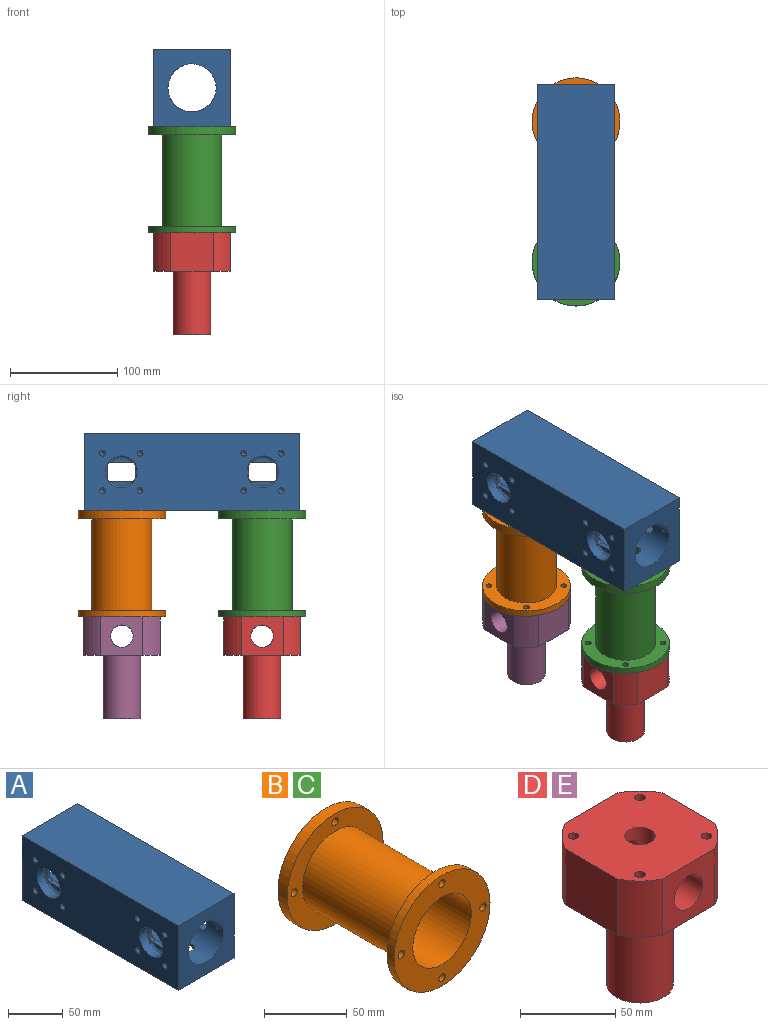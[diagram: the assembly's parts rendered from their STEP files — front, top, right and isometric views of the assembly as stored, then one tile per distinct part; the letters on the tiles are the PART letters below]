
ASSEMBLY  parts=5 mates=10
PART A: 165 faces, bbox 72.3x201.3x72.3 mm
  f0: cylinder r=22.5mm len=201mm, axis (0,-1,0), area 25576.7mm2, adj f1,f114,f115,f116,f117,f118,f119,f120
  f1: cone r=0mm half-angle=59deg, axis (1,0,0), area 3.6mm2, adj f0,f2
  f2: cylinder r=1mm len=10mm, axis (1,0,0), area 62.8mm2, adj f1,f3
  f3: cone r=1mm half-angle=45deg, axis (1,0,0), area 66.6mm2, adj f2,f4
  f4: plane 201.02x72.02mm, normal (1,0,0), area 12119.6mm2, adj f3,f5,f85,f86,f87,f88,f89,f90
  f5: plane 201x72mm, normal (0,0,-1), area 9355.9mm2, adj f4,f6,f53,f58,f63,f65,f67,f69
  f6: plane 201x72mm, normal (-1,0,0), area 12868.2mm2, adj f5,f7,f22,f37,f39,f41,f43,f45
  f7: cylinder r=15mm len=30mm, axis (-1,0,0), area 862.6mm2, adj f6,f8,f9,f11,f12,f13,f14,f15
  f8: bspline ~2.82x2.43mm, area 2.1mm2, adj f7,f9,f21,f159
  f9: torus R=13mm, axis (-1,0,0), area 72.2mm2, adj f7,f8,f10,f11
  f10: plane 18.74x3.99mm, normal (-1,0,0), area 51.6mm2, adj f9,f159
  f11: bspline ~2.87x2.49mm, area 2.1mm2, adj f7,f9,f12,f159
  f12: bspline ~3.64x3.35mm, area 6.1mm2, adj f7,f11,f13,f158
  f13: bspline ~14.54x2mm, area 35.1mm2, adj f7,f12,f14,f157
  f14: bspline ~3.66x3.36mm, area 6.2mm2, adj f7,f13,f15,f156
  f15: bspline ~2.82x2.43mm, area 2mm2, adj f7,f14,f16,f155
  f16: torus R=13mm, axis (-1,0,0), area 72.4mm2, adj f7,f15,f17,f18
  f17: plane 18.78x4.01mm, normal (-1,0,0), area 52mm2, adj f16,f155
  f18: bspline ~2.86x2.49mm, area 2mm2, adj f7,f16,f19,f155
  f19: bspline ~3.66x3.36mm, area 6.2mm2, adj f7,f18,f20,f162
  f20: bspline ~14.54x2mm, area 35.1mm2, adj f7,f19,f21,f161
  f21: bspline ~4.35x3.75mm, area 6.1mm2, adj f7,f8,f20,f160
  f22: cylinder r=15mm len=30mm, axis (-1,0,0), area 862.6mm2, adj f6,f23,f24,f26,f27,f28,f29,f30
  f23: bspline ~2.82x2.43mm, area 2.1mm2, adj f22,f24,f36,f140
  f24: torus R=13mm, axis (-1,0,0), area 72.2mm2, adj f22,f23,f25,f26
  f25: plane 18.74x3.99mm, normal (-1,0,0), area 51.6mm2, adj f24,f140
  f26: bspline ~2.87x2.49mm, area 2.1mm2, adj f22,f24,f27,f140
  f27: bspline ~3.64x3.35mm, area 6.1mm2, adj f22,f26,f28,f139
  f28: bspline ~14.54x2mm, area 35.1mm2, adj f22,f27,f29,f146
  f29: bspline ~3.66x3.36mm, area 6.2mm2, adj f22,f28,f30,f145
  f30: bspline ~2.82x2.43mm, area 2mm2, adj f22,f29,f31,f144
  f31: torus R=13mm, axis (-1,0,0), area 72.4mm2, adj f22,f30,f32,f33
  f32: plane 18.78x4.01mm, normal (-1,0,0), area 52mm2, adj f31,f144
  f33: bspline ~2.86x2.49mm, area 2mm2, adj f22,f31,f34,f144
  f34: bspline ~3.66x3.36mm, area 6.2mm2, adj f22,f33,f35,f143
  f35: bspline ~14.54x2mm, area 35.1mm2, adj f22,f34,f36,f142
  f36: bspline ~4.35x3.75mm, area 6.1mm2, adj f22,f23,f35,f141
  f37: cylinder r=2.75mm len=13mm, axis (-1,0,0), area 224.6mm2, adj f6,f38
  f38: cone r=0mm half-angle=59deg, axis (-1,0,0), area 27.7mm2, adj f37
  f39: cylinder r=2.75mm len=13mm, axis (-1,0,0), area 224.6mm2, adj f6,f40
  f40: cone r=0mm half-angle=59deg, axis (-1,0,0), area 27.7mm2, adj f39
  f41: cylinder r=2.75mm len=13mm, axis (-1,0,0), area 224.6mm2, adj f6,f42
  f42: cone r=0mm half-angle=59deg, axis (-1,0,0), area 27.7mm2, adj f41
  f43: cylinder r=2.75mm len=13mm, axis (-1,0,0), area 224.6mm2, adj f6,f44
  f44: cone r=0mm half-angle=59deg, axis (-1,0,0), area 27.7mm2, adj f43
  f45: cylinder r=2.75mm len=13mm, axis (-1,0,0), area 224.6mm2, adj f6,f46
  f46: cone r=0mm half-angle=59deg, axis (-1,0,0), area 27.7mm2, adj f45
  f47: cylinder r=2.75mm len=13mm, axis (-1,0,0), area 224.6mm2, adj f6,f48
  f48: cone r=0mm half-angle=59deg, axis (-1,0,0), area 27.7mm2, adj f47
  f49: cylinder r=2.75mm len=13mm, axis (-1,0,0), area 224.6mm2, adj f6,f50
  f50: cone r=0mm half-angle=59deg, axis (-1,0,0), area 27.7mm2, adj f49
  f51: cylinder r=2.75mm len=13mm, axis (-1,0,0), area 224.6mm2, adj f6,f52
  f52: cone r=0mm half-angle=59deg, axis (-1,0,0), area 27.7mm2, adj f51
  f53: cylinder r=28mm len=56mm, axis (0,0,-1), area 439.8mm2, adj f5,f54
  f54: plane 56x56mm, normal (0,0,-1), area 87.2mm2, adj f53,f55
  f55: torus R=26mm, axis (0,0,-1), area 769.8mm2, adj f54,f56
  f56: plane 49x49mm, normal (0,0,-1), area 382.9mm2, adj f55,f57
  f57: cone r=24.52mm half-angle=46.5deg, axis (0,0,-1), area 1437.8mm2, adj f56,f131,f132,f133,f134,f135,f136,f137
  f58: cylinder r=28mm len=56mm, axis (0,0,-1), area 439.8mm2, adj f5,f59
  f59: plane 56x56mm, normal (0,0,-1), area 87.2mm2, adj f58,f60
  f60: torus R=26mm, axis (0,0,-1), area 769.8mm2, adj f59,f61
  f61: plane 49x49mm, normal (0,0,-1), area 382.9mm2, adj f60,f62
  f62: cone r=24.52mm half-angle=46.5deg, axis (0,0,-1), area 1437.8mm2, adj f61,f123,f124,f125,f126,f127,f128,f129
  f63: cylinder r=2.75mm len=15mm, axis (0,0,-1), area 224.6mm2, adj f5,f64,f99
  f64: cone r=0mm half-angle=59deg, axis (0,0,-1), area 23.4mm2, adj f63,f99
  f65: cylinder r=2.75mm len=15mm, axis (0,0,-1), area 259.2mm2, adj f5,f66
  f66: cone r=0mm half-angle=59deg, axis (0,0,-1), area 27.7mm2, adj f65
  f67: cylinder r=2.75mm len=15mm, axis (0,0,-1), area 259.2mm2, adj f5,f68
  f68: cone r=0mm half-angle=59deg, axis (0,0,-1), area 27.7mm2, adj f67
  f69: cylinder r=2.75mm len=15mm, axis (0,0,-1), area 203.8mm2, adj f5,f70,f72,f73,f98
  f70: cone r=0mm half-angle=59deg, axis (0,0,-1), area 19mm2, adj f69,f71,f98
  f71: cylinder r=2.75mm len=2.49mm, axis (0,0,-1), area 0mm2, adj f70,f98
  f72: cylinder r=2.75mm len=0.48mm, axis (1,0,0), area 0mm2, adj f69,f73,f98
  f73: cone r=0mm half-angle=59deg, axis (1,0,0), area 27.7mm2, adj f69,f72,f98
  f74: cylinder r=2.75mm len=15mm, axis (0,0,-1), area 224.6mm2, adj f5,f75,f101
  f75: cone r=0mm half-angle=59deg, axis (0,0,-1), area 23.4mm2, adj f74,f101
  f76: cylinder r=2.75mm len=15mm, axis (0,0,-1), area 259.2mm2, adj f5,f77
  f77: cone r=0mm half-angle=59deg, axis (0,0,-1), area 27.7mm2, adj f76
  f78: cylinder r=2.75mm len=15mm, axis (0,0,-1), area 259.2mm2, adj f5,f79
  f79: cone r=0mm half-angle=59deg, axis (0,0,-1), area 27.7mm2, adj f78
  f80: cylinder r=2.75mm len=15mm, axis (0,0,-1), area 203.8mm2, adj f5,f81,f82,f84,f103
  f81: cylinder r=2.75mm len=0.48mm, axis (1,0,0), area 0mm2, adj f80,f84,f103
  f82: cone r=0mm half-angle=59deg, axis (0,0,-1), area 19mm2, adj f80,f83,f103
  f83: cylinder r=2.75mm len=2.49mm, axis (0,0,-1), area 0mm2, adj f82,f103
  f84: cone r=0mm half-angle=59deg, axis (1,0,0), area 27.7mm2, adj f80,f81,f103
  f85: plane 201x72mm, normal (0,0,1), area 14472mm2, adj f4,f6,f163,f164
  f86: cone r=17.5mm half-angle=43.4deg, axis (1,0,0), area 730.9mm2, adj f4,f87,f147,f148,f149,f150,f151,f152
  f87: cone r=17.5mm half-angle=48.8deg, axis (1,0,0), area 0mm2, adj f4,f86
  f88: cone r=17.5mm half-angle=43.4deg, axis (1,0,0), area 730.9mm2, adj f4,f89,f115,f116,f117,f118,f119,f120
  f89: cone r=17.5mm half-angle=48.8deg, axis (1,0,0), area 0mm2, adj f4,f88
  f90: cylinder r=2.75mm len=14mm, axis (1,0,0), area 241.9mm2, adj f4,f91
  f91: cone r=0mm half-angle=59deg, axis (1,0,0), area 27.7mm2, adj f90
  f92: cylinder r=2.75mm len=14mm, axis (1,0,0), area 241.9mm2, adj f4,f93
  f93: cone r=0mm half-angle=59deg, axis (1,0,0), area 27.7mm2, adj f92
  f94: cylinder r=2.75mm len=14mm, axis (1,0,0), area 241.9mm2, adj f4,f95
  f95: cone r=0mm half-angle=59deg, axis (1,0,0), area 27.7mm2, adj f94
  f96: cylinder r=2.75mm len=14mm, axis (1,0,0), area 241.9mm2, adj f4,f97
  f97: cone r=0mm half-angle=59deg, axis (1,0,0), area 27.7mm2, adj f96
  f98: cylinder r=2.75mm len=14mm, axis (1,0,0), area 191mm2, adj f4,f69,f70,f71,f72,f73
  f99: cylinder r=2.75mm len=14mm, axis (1,0,0), area 207.5mm2, adj f4,f63,f64,f100
  f100: cone r=0mm half-angle=59deg, axis (1,0,0), area 27.7mm2, adj f99
  f101: cylinder r=2.75mm len=14mm, axis (1,0,0), area 207.4mm2, adj f4,f74,f75,f102
  f102: cone r=0mm half-angle=59deg, axis (1,0,0), area 27.7mm2, adj f101
  f103: cylinder r=2.75mm len=14mm, axis (1,0,0), area 191mm2, adj f4,f80,f81,f82,f83,f84
  f104: cone r=1mm half-angle=45deg, axis (1,0,0), area 66.6mm2, adj f4,f105
  f105: cylinder r=1mm len=10mm, axis (1,0,0), area 62.8mm2, adj f104,f114
  f106: cylinder r=3.3mm len=15mm, axis (1,0,0), area 311mm2, adj f4,f107
  f107: cone r=0mm half-angle=59deg, axis (1,0,0), area 39.9mm2, adj f106
  f108: cylinder r=3.3mm len=15mm, axis (1,0,0), area 311mm2, adj f4,f109
  f109: cone r=0mm half-angle=59deg, axis (1,0,0), area 39.9mm2, adj f108
  f110: cylinder r=3.3mm len=15mm, axis (1,0,0), area 311mm2, adj f4,f111
  f111: cone r=0mm half-angle=59deg, axis (1,0,0), area 39.9mm2, adj f110
  f112: cylinder r=3.3mm len=15mm, axis (1,0,0), area 311mm2, adj f4,f113
  f113: cone r=0mm half-angle=59deg, axis (1,0,0), area 39.9mm2, adj f112
  f114: cone r=0mm half-angle=59deg, axis (1,0,0), area 3.6mm2, adj f0,f105
  f115: plane 12.01x10.96mm, normal (0,-1,0), area 113.7mm2, adj f0,f88,f116,f122
  f116: cylinder r=3mm len=12.01mm, axis (-1,0,0), area 51.9mm2, adj f0,f88,f115,f117
  f117: plane 20.01x11.11mm, normal (0,0,-1), area 161.7mm2, adj f0,f88,f116,f118
  f118: cylinder r=3mm len=12.01mm, axis (-1,0,0), area 51.9mm2, adj f0,f88,f117,f119
  f119: plane 12.01x10.96mm, normal (0,1,0), area 113.7mm2, adj f0,f88,f118,f120
  f120: cylinder r=3mm len=12.01mm, axis (-1,0,0), area 51.9mm2, adj f0,f88,f119,f121
  f121: plane 20.01x11.1mm, normal (0,0,1), area 161.5mm2, adj f0,f88,f120,f122
  f122: cylinder r=3mm len=12.01mm, axis (-1,0,0), area 51.9mm2, adj f0,f88,f115,f121
  f123: cylinder r=3mm len=5.7mm, axis (0,0,-1), area 22.4mm2, adj f0,f62,f124,f130
  f124: plane 20.01x4.89mm, normal (1,0,0), area 43.6mm2, adj f0,f62,f123,f125
  f125: cylinder r=3mm len=5.7mm, axis (0,0,-1), area 22.4mm2, adj f0,f62,f124,f126
  f126: plane 12.01x4.64mm, normal (0,-1,0), area 39.2mm2, adj f0,f62,f125,f127
  f127: cylinder r=3mm len=5.7mm, axis (0,0,-1), area 22.4mm2, adj f0,f62,f126,f128
  f128: plane 20.01x4.89mm, normal (-1,0,0), area 43.6mm2, adj f0,f62,f127,f129
  f129: cylinder r=3mm len=5.7mm, axis (0,0,-1), area 22.4mm2, adj f0,f62,f128,f130
  f130: plane 12.01x4.64mm, normal (0,1,0), area 39.2mm2, adj f0,f62,f123,f129
  f131: cylinder r=3mm len=5.7mm, axis (0,0,-1), area 22.4mm2, adj f0,f57,f132,f138
  f132: plane 20.01x4.89mm, normal (1,0,0), area 43.6mm2, adj f0,f57,f131,f133
  f133: cylinder r=3mm len=5.7mm, axis (0,0,-1), area 22.4mm2, adj f0,f57,f132,f134
  f134: plane 12.01x4.64mm, normal (0,-1,0), area 39.2mm2, adj f0,f57,f133,f135
  f135: cylinder r=3mm len=5.7mm, axis (0,0,-1), area 22.4mm2, adj f0,f57,f134,f136
  f136: plane 20.01x4.89mm, normal (-1,0,0), area 43.6mm2, adj f0,f57,f135,f137
  f137: cylinder r=3mm len=5.7mm, axis (0,0,-1), area 22.4mm2, adj f0,f57,f136,f138
  f138: plane 12.01x4.64mm, normal (0,1,0), area 39.2mm2, adj f0,f57,f131,f137
  f139: cylinder r=3mm len=4.38mm, axis (-1,0,0), area 18.1mm2, adj f0,f27,f140,f146
  f140: plane 20.02x4.4mm, normal (0,0,-1), area 87.6mm2, adj f0,f23,f25,f26,f139,f141
  f141: cylinder r=3mm len=4.38mm, axis (-1,0,0), area 18.1mm2, adj f0,f36,f140,f142
  f142: plane 12.26x3.57mm, normal (0,-1,0), area 33.2mm2, adj f0,f35,f141,f143
  f143: cylinder r=3mm len=4.37mm, axis (-1,0,0), area 18.1mm2, adj f0,f34,f142,f144
  f144: plane 20.02x4.39mm, normal (0,0,1), area 87.5mm2, adj f0,f30,f32,f33,f143,f145
  f145: cylinder r=3mm len=4.37mm, axis (-1,0,0), area 18.1mm2, adj f0,f29,f144,f146
  f146: plane 12.25x3.57mm, normal (0,1,0), area 33.2mm2, adj f0,f28,f139,f145
  f147: cylinder r=3mm len=12.01mm, axis (-1,0,0), area 51.9mm2, adj f0,f86,f148,f154
  f148: plane 12.01x10.96mm, normal (0,1,0), area 113.7mm2, adj f0,f86,f147,f149
  f149: cylinder r=3mm len=12.01mm, axis (-1,0,0), area 51.9mm2, adj f0,f86,f148,f150
  f150: plane 20.01x11.1mm, normal (0,0,1), area 161.5mm2, adj f0,f86,f149,f151
  f151: cylinder r=3mm len=12.01mm, axis (-1,0,0), area 51.9mm2, adj f0,f86,f150,f152
  f152: plane 12.01x10.96mm, normal (0,-1,0), area 113.7mm2, adj f0,f86,f151,f153
  f153: cylinder r=3mm len=12.01mm, axis (-1,0,0), area 51.9mm2, adj f0,f86,f152,f154
  f154: plane 20.01x11.11mm, normal (0,0,-1), area 161.6mm2, adj f0,f86,f147,f153
  f155: plane 20.02x4.39mm, normal (0,0,1), area 87.5mm2, adj f0,f15,f17,f18,f156,f162
  f156: cylinder r=3mm len=4.37mm, axis (-1,0,0), area 18.1mm2, adj f0,f14,f155,f157
  f157: plane 12.25x3.57mm, normal (0,1,0), area 33.2mm2, adj f0,f13,f156,f158
  f158: cylinder r=3mm len=4.38mm, axis (-1,0,0), area 18.1mm2, adj f0,f12,f157,f159
  f159: plane 20.02x4.4mm, normal (0,0,-1), area 87.6mm2, adj f0,f8,f10,f11,f158,f160
  f160: cylinder r=3mm len=4.38mm, axis (-1,0,0), area 18.1mm2, adj f0,f21,f159,f161
  f161: plane 12.26x3.57mm, normal (0,-1,0), area 33.2mm2, adj f0,f20,f160,f162
  f162: cylinder r=3mm len=4.37mm, axis (-1,0,0), area 18.1mm2, adj f0,f19,f155,f161
  f163: plane 72x72mm, normal (0,1,0), area 3593.6mm2, adj f0,f4,f5,f6,f85
  f164: plane 72x72mm, normal (0,-1,0), area 3593.6mm2, adj f0,f4,f5,f6,f85
PART B: 16 faces, bbox 82x99.5x82 mm
  f0: cylinder r=41mm len=82mm, axis (0,1,0), area 2060.9mm2, adj f1,f2
  f1: plane 82x82mm, normal (0,-1,0), area 2723mm2, adj f0,f3,f12,f13,f14,f15
  f2: plane 82x82mm, normal (0,1,0), area 3222.5mm2, adj f0,f7,f12,f13,f14,f15
  f3: cylinder r=28mm len=85.5mm, axis (0,1,0), area 15041.9mm2, adj f1,f6
  f4: cylinder r=41mm len=82mm, axis (0,1,0), area 1545.7mm2, adj f5,f6
  f5: plane 82x82mm, normal (0,-1,0), area 3222.5mm2, adj f4,f7,f8,f9,f10,f11
  f6: plane 82x82mm, normal (0,1,0), area 2723mm2, adj f3,f4,f8,f9,f10,f11
  f7: cylinder r=25mm len=99.5mm, axis (0,-1,0), area 15629.4mm2, adj f2,f5
  f8: cylinder r=2.75mm len=6mm, axis (0,-1,0), area 103.7mm2, adj f5,f6
  f9: cylinder r=2.75mm len=6mm, axis (0,-1,0), area 103.7mm2, adj f5,f6
  f10: cylinder r=2.75mm len=6mm, axis (0,-1,0), area 103.7mm2, adj f5,f6
  f11: cylinder r=2.75mm len=6mm, axis (0,-1,0), area 103.7mm2, adj f5,f6
  f12: cylinder r=2.75mm len=8mm, axis (0,-1,0), area 138.2mm2, adj f1,f2
  f13: cylinder r=2.75mm len=8mm, axis (0,-1,0), area 138.2mm2, adj f1,f2
  f14: cylinder r=2.75mm len=8mm, axis (0,-1,0), area 138.2mm2, adj f1,f2
  f15: cylinder r=2.75mm len=8mm, axis (0,-1,0), area 138.2mm2, adj f1,f2
PART C: same geometry as B
PART D: 23 faces, bbox 72x72x95 mm
  f0: cylinder r=8mm len=16mm, axis (0,0,-1), area 465mm2, adj f10,f22
  f1: cylinder r=8mm len=70.2mm, axis (0,0,-1), area 3430.6mm2, adj f21,f22
  f2: plane 39.24x36mm, normal (0,-1,0), area 1066.4mm2, adj f3,f9,f10,f11,f22
  f3: cylinder r=41mm len=36mm, axis (0,0,-1), area 845.4mm2, adj f2,f4,f10,f11
  f4: plane 39.24x36mm, normal (1,0,0), area 1412.7mm2, adj f3,f5,f10,f11
  f5: cylinder r=41mm len=36mm, axis (0,0,-1), area 845.4mm2, adj f4,f6,f10,f11
  f6: plane 39.24x36mm, normal (0,1,0), area 1066.4mm2, adj f5,f7,f10,f11,f22
  f7: cylinder r=41mm len=36mm, axis (0,0,-1), area 845.4mm2, adj f6,f8,f10,f11
  f8: plane 39.24x36mm, normal (-1,0,0), area 1412.7mm2, adj f7,f9,f10,f11
  f9: cylinder r=41mm len=36mm, axis (0,0,-1), area 845.4mm2, adj f2,f8,f10,f11
  f10: plane 72x72mm, normal (0,0,1), area 4455mm2, adj f0,f2,f3,f4,f5,f6,f7,f8
  f11: plane 72x72mm, normal (0,0,-1), area 3788.9mm2, adj f2,f3,f4,f5,f6,f7,f8,f9
  f12: cylinder r=2.75mm len=10mm, axis (0,0,1), area 172.8mm2, adj f10,f13
  f13: cone r=0mm half-angle=59deg, axis (0,0,1), area 27.7mm2, adj f12
  f14: cylinder r=2.75mm len=10mm, axis (0,0,1), area 172.8mm2, adj f10,f15
  f15: cone r=0mm half-angle=59deg, axis (0,0,1), area 27.7mm2, adj f14
  f16: cylinder r=2.75mm len=10mm, axis (0,0,1), area 172.8mm2, adj f10,f17
  f17: cone r=0mm half-angle=59deg, axis (0,0,1), area 27.7mm2, adj f16
  f18: cylinder r=2.75mm len=10mm, axis (0,0,1), area 172.8mm2, adj f10,f19
  f19: cone r=0mm half-angle=59deg, axis (0,0,1), area 27.7mm2, adj f18
  f20: cylinder r=17.5mm len=59mm, axis (0,0,1), area 6487.4mm2, adj f11,f21
  f21: plane 35x35mm, normal (0,0,-1), area 761.1mm2, adj f1,f20
  f22: cylinder r=10.5mm len=72mm, axis (0,1,0), area 4309.6mm2, adj f0,f1,f2,f6
PART E: same geometry as D
PLACE A at identity fixed
PLACE B rot(axis=(0.28,0.68,0.68),148.6deg) t=(-72,-35,36)mm
PLACE C rot(axis=(0.86,0.36,0.36),98.4deg) t=(-72,-166,36)mm
PLACE D rot(axis=(0,0,-1),90deg) t=(-72,-166,-99.5)mm
PLACE E rot(axis=(0,0,1),90deg) t=(-72,-35,-99.5)mm
MATE planar B.f0 <-> E.f0  axis (0,0,-1) through (-72,-35,-63.5)mm
MATE planar D.f22 <-> E.f22  axis (-1,0,0) through (-108,-166,-81.5)mm
MATE cylindrical B.f0 <-> E.f0  axis (0,0,-1) through (-72,-35,-13.75)mm
MATE revolute A.f80 <-> B.f10  axis (0,0,-1) through (-47.25,-10.25,36)mm
MATE planar A.f4 <-> D.f22  axis (1,0,0) through (-36,-100.5,71.95)mm
MATE revolute A.f63 <-> C.f9  axis (0,0,-1) through (-47.25,-141.25,36)mm
MATE revolute B.f9 <-> A.f79  axis (0,0,1) through (-96.75,-10.25,36)mm
MATE revolute C.f10 <-> A.f69  axis (0,0,1) through (-47.25,-190.75,36)mm
MATE planar C.f0 <-> D.f0  axis (0,0,-1) through (-72,-166,-63.5)mm
MATE cylindrical D.f0 <-> C.f0  axis (0,0,1) through (-72,-166,-129)mm
